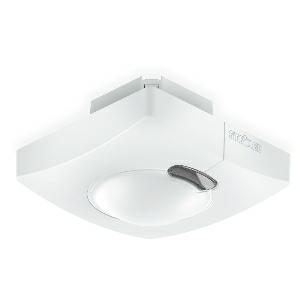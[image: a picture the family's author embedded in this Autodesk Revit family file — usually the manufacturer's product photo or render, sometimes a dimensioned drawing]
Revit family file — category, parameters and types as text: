
# Revit family: hf_3360_033743
name_source: partatom
category: Elektroinstallationen
revit_build: Autodesk Revit 2016 (Build: 20190508_0715(x64)
units: mm (PartAtom-declared; Revit-internal decimal feet)

## family parameters
Basisbauteil = Fläche
Beim Laden mit Abzugskörper schneiden = Nein
Bemaßung runder Anschluss = Durchmesser verwenden
Beschriftungsausrichtung beibehalten = Nein
Gemeinsam genutzt = Nein
Raumberechnungspunkt = Nein
Teiletyp = Normal

## types (1)
- HF 3360
    Apparent Load = 0 VA
    Beschreibung = Type: Motion detectors; Dimensions (L x W x H): 64 x 94 x 94 mm; Mains power supply: 220 – 240 V / 50 – 60 Hz; Sensor Technology: High frequency; Application, place: Indoors; Application, room: function room / ancillary room, stairwell, WC / washroom, multi-storey / underground car park, Indoors; Installation site: wall, ceiling, corner; Installation: Concealed wiring; HF-system: 5,8 GHz; Electronic scalability: Yes; Mechanical scalability: No; Mounting height: 2,00 – 4,00 m; Optimum mounting height: 2,8 m; Detection: also through glass, wood and stud walls; Detection angle: 360 °; Angle of aperture: 140 °; Sneak-by guard: Yes; Reach, radial: Ø 8 m (50 m²); Reach, tangential: Ø 8 m (50 m²); Twilight setting TEACH: Yes; Twilight setting: 2 – 1000 lx; Time setting: 5 sec – 15 min; Control output, Dali: Broadcast 1x30 electronic ballasts; Constant-lighting control: Yes; Basic light level function: Yes; Basic light level function in per cent: 10 – 50 %; Basic light level function time: 1-30 min, all night; Basic light level function percentage, from: 10 %; Basic light level function percentage, up to: 50 %; Functions: Normal / test mode, Manual ON / ON-OFF, Constant-lighting control ON-OFF; Settings via: Remote control, Potentiometers, Smart Remote; With remote control: No; Interconnection: Yes; IP-rating: IP20; Material: Plastic; Ambient temperature: -20 – 50 °C; Colour: white; Colour, RAL: 9003; Manufacturer's Warranty: 5 years; Version: DALI-2 Application Controller - concealed, sq.; PU1, EAN: 4007841033743
    Height = 94 mm  [stored 0.308399 ft]
    Hersteller = Steinel
    Length = 64 mm
    ModVariant = Nein
    Modell = 033743
    Mounting Type = Recessed
    Number of Poles = 1
    OnlyDefault = Ja
    Power Factor = 1
    Product Name = HF 3360
    Product group = Sensor-switched indoor light
    ProductGroupID = 30
    Protection Class = Protection class
    Protection Degree = IP 20
    RlxData = <blob elided: 27245 chars, md5=40375096>
    SensorDataFile = {"IESDataFiles":[]}
    Typenbild = produkt1_033743.jpg
    Typenkommentare = Product without accessories
    URL = http://relux.com
    VarID = ---
    Voltage = 0 V
    Vorgabe-Ansicht = 1800 mm
    Weight = 0.00 kg
    Width = 94 mm  [stored 0.308399 ft]

note: [stored X ft] marks values corroborated as IEEE doubles in the binary element streams (Revit-internal decimal feet)

## geometry (parser evidence)
native form markers: Blend x4, Sweep x11
no freeform markers — native parametric forms only
